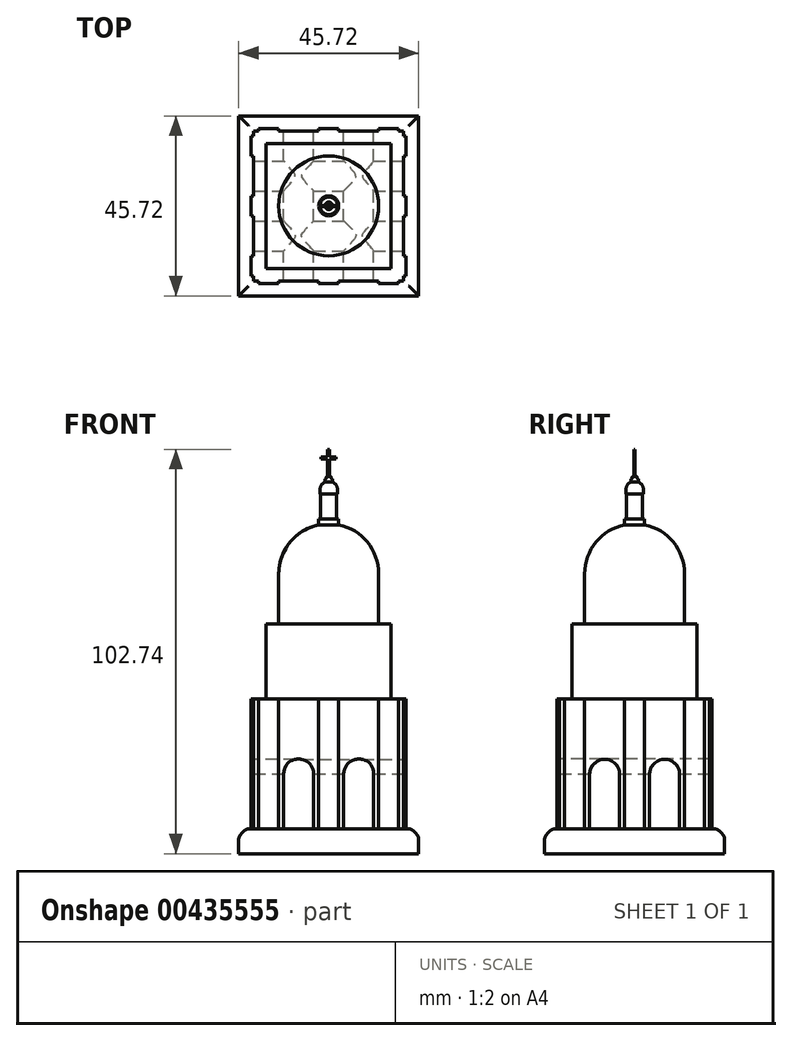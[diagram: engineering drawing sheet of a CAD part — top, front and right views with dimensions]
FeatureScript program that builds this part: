
annotation { "Feature Type Name" : "Feature", "Feature Type Description" : "" }
export const myFeature = defineFeature(function(context is Context, id is Id, definition is map)
    precondition{}
    {
        {
            var Q0;
            Q0=qCreatedBy(makeId("Top.planeOp"),FACE);
            var sketch = newSketch(context, id + "F0", { "sketchPlane" : qUnion([Q0])});
            skLineSegment(sketch, "E0.bottom", {"start": v(-19.05, -19.05) * mm, "end": v(19.05, -19.05) * mm});
            skLineSegment(sketch, "E0.top", {"start": v(-19.05, 19.05) * mm, "end": v(19.05, 19.05) * mm});
            skLineSegment(sketch, "E0.left", {"start": v(-19.05, -19.05) * mm, "end": v(-19.05, 19.05) * mm});
            skLineSegment(sketch, "E0.right", {"start": v(19.05, -19.05) * mm, "end": v(19.05, 19.05) * mm});
            skPoint(sketch, "E0.middle", {"position": v(0, 0) * mm});
            skLineSegment(sketch, "E1.bottom", {"start": v(-19.05, -19.05) * mm, "end": v(-11.43, -19.05) * mm});
            skLineSegment(sketch, "E1.left", {"start": v(-19.05, -19.05) * mm, "end": v(-19.05, -18.14) * mm});
            skLineSegment(sketch, "E2.bottom", {"start": v(-11.43, -19.05) * mm, "end": v(-3.8, -19.05) * mm});
            skLineSegment(sketch, "E3.bottom", {"start": v(-3.8, -19.05) * mm, "end": v(3.81, -19.05) * mm});
            skLineSegment(sketch, "E4.bottom", {"start": v(3.81, -19.05) * mm, "end": v(11.43, -19.05) * mm});
            skSolve(sketch);
        }
        {
            var Q0;
            Q0=makeQuery(id+"F0.imprint","IMPRINT",FACE,{"disambiguationData":[TD([[makeQuery(id+"F0.imprint","IMPRINT",EDGE,{"derivedFrom":sQuery(id+"F0.wireOp",EDGE,"E0.bottom")}),1.0]])]});
            extrude(context, id + "F1", {"entities" : qUnion([Q0]), "depth" : 38.1 * mm});
        }
        {
            var Q0;
            Q0=makeQuery(id+"F1.opExtrude","CAP_FACE",FACE,{"disambiguationData":[OSD([sQuery(id+"F0.wireOp",EDGE,"E0.bottom"),sQuery(id+"F0.wireOp",EDGE,"E0.top"),sQuery(id+"F0.wireOp",EDGE,"E0.left"),sQuery(id+"F0.wireOp",EDGE,"E0.right")])],"isStart":false});
            var sketch = newSketch(context, id + "F2", { "sketchPlane" : qUnion([Q0])});
            skLineSegment(sketch, "E5.bottom", {"start": v(-15.88, -15.88) * mm, "end": v(15.88, -15.88) * mm});
            skLineSegment(sketch, "E5.top", {"start": v(-15.88, 15.88) * mm, "end": v(15.88, 15.88) * mm});
            skLineSegment(sketch, "E5.left", {"start": v(-15.88, -15.88) * mm, "end": v(-15.88, 15.88) * mm});
            skLineSegment(sketch, "E5.right", {"start": v(15.88, -15.88) * mm, "end": v(15.88, 15.88) * mm});
            skPoint(sketch, "E5.middle", {"position": v(0, 0) * mm});
            skSolve(sketch);
        }
        {
            var Q0;
            Q0 = qSketchRegion(id + "F2", true);
            extrude(context, id + "F3", {"entities" : qUnion([Q0]), "operationType" : NewBodyOperationType.ADD, "depth" : 19.05 * mm});
        }
        {
            var Q0;
            Q0=makeQuery(id+"F3.opExtrude","CAP_FACE",FACE,{"disambiguationData":[OSD([sQuery(id+"F2.wireOp",EDGE,"E5.bottom"),sQuery(id+"F2.wireOp",EDGE,"E5.top"),sQuery(id+"F2.wireOp",EDGE,"E5.left"),sQuery(id+"F2.wireOp",EDGE,"E5.right")])],"isStart":false});
            var sketch = newSketch(context, id + "F4", { "sketchPlane" : qUnion([Q0])});
            skCircle(sketch, "E6", {"center": v(0, 0) * mm, "radius": 12.7 * mm});
            skSolve(sketch);
        }
        {
            var Q0;
            Q0 = qSketchRegion(id + "F4", true);
            extrude(context, id + "F5", {"entities" : qUnion([Q0]), "operationType" : NewBodyOperationType.ADD, "depth" : 25.4 * mm});
        }
        {
            var Q0;
            Q0=makeQuery(id+"F5.opExtrude","CAP_FACE",FACE,{"disambiguationData":[OSD([sQuery(id+"F4.wireOp",EDGE,"E6")])],"isStart":false});
            fillet(context, id + "F6", {"entities" : qUnion([Q0]), "radius" : 12.7 * mm, "tangentPropagation" : true, "allowEdgeOverflow" : false});
        }
        {
            var Q0;
            Q0=makeQuery(id+"F3.opExtrude","CAP_FACE",FACE,{"disambiguationData":[OSD([sQuery(id+"F2.wireOp",EDGE,"E5.bottom"),sQuery(id+"F2.wireOp",EDGE,"E5.top"),sQuery(id+"F2.wireOp",EDGE,"E5.left"),sQuery(id+"F2.wireOp",EDGE,"E5.right")])],"isStart":false});
            var sketch = newSketch(context, id + "F7", { "sketchPlane" : qUnion([Q0])});
            skCircle(sketch, "E7", {"center": v(0, 0) * mm, "radius": 2.54 * mm});
            skSolve(sketch);
        }
        {
            var Q0;
            Q0 = qSketchRegion(id + "F7", true);
            extrude(context, id + "F8", {"entities" : qUnion([Q0]), "operationType" : NewBodyOperationType.ADD, "depth" : 26.67 * mm});
        }
        {
            var Q0;
            Q0=makeQuery(id+"F8.opExtrude","CAP_FACE",FACE,{"disambiguationData":[OSD([sQuery(id+"F7.wireOp",EDGE,"E7")])],"isStart":false});
            var sketch = newSketch(context, id + "F9", { "sketchPlane" : qUnion([Q0])});
            skCircle(sketch, "E8", {"center": v(0, 0) * mm, "radius": 2.03 * mm});
            skSolve(sketch);
        }
        {
            var Q0;
            Q0 = qSketchRegion(id + "F9", true);
            extrude(context, id + "F10", {"entities" : qUnion([Q0]), "operationType" : NewBodyOperationType.ADD, "depth" : 6.35 * mm});
        }
        {
            var Q0;
            Q0=makeQuery(id+"F10.opExtrude","CAP_FACE",FACE,{"disambiguationData":[OSD([sQuery(id+"F9.wireOp",EDGE,"E8")])],"isStart":false});
            var sketch = newSketch(context, id + "F11", { "sketchPlane" : qUnion([Q0])});
            skCircle(sketch, "E9", {"center": v(0, 0) * mm, "radius": 2.22 * mm});
            skSolve(sketch);
        }
        {
            var Q0;
            Q0 = qSketchRegion(id + "F11", true);
            extrude(context, id + "F12", {"entities" : qUnion([Q0]), "operationType" : NewBodyOperationType.ADD, "depth" : 3.05 * mm});
        }
        {
            var Q0;
            Q0=makeQuery(id+"F12.opExtrude","CAP_FACE",FACE,{"disambiguationData":[OSD([sQuery(id+"F11.wireOp",EDGE,"E9")])],"isStart":false});
            fillet(context, id + "F13", {"entities" : qUnion([Q0]), "radius" : 1.9 * mm, "tangentPropagation" : true, "allowEdgeOverflow" : false});
        }
        {
            var Q0;
            Q0=makeQuery(id+"F12.opExtrude","CAP_FACE",FACE,{"disambiguationData":[OSD([sQuery(id+"F11.wireOp",EDGE,"E9")])],"isStart":false});
            var sketch = newSketch(context, id + "F14", { "sketchPlane" : qUnion([Q0])});
            skCircle(sketch, "E10", {"center": v(0, 0) * mm, "radius": 0.95 * mm});
            skSolve(sketch);
        }
        {
            var Q0;
            Q0 = qSketchRegion(id + "F14", true);
            extrude(context, id + "F15", {"entities" : qUnion([Q0]), "operationType" : NewBodyOperationType.ADD, "depth" : 0.76 * mm});
        }
        {
            var Q0;
            Q0=makeQuery(id+"F15.opExtrude","CAP_FACE",FACE,{"disambiguationData":[OSD([sQuery(id+"F14.wireOp",EDGE,"E10")])],"isStart":false});
            var Q1;
            Q1=makeQuery(id+"F15.opExtrude","SWEPT_FACE",FACE,{"disambiguationData":[OSD([sQuery(id+"F14.wireOp",EDGE,"E10")])]});
            fillet(context, id + "F16", {"entities" : qUnion([Q0, Q1]), "radius" : 0.25 * mm, "tangentPropagation" : true, "allowEdgeOverflow" : false});
        }
        {
            var Q0;
            Q0=makeQuery(id+"F15.opExtrude","CAP_FACE",FACE,{"disambiguationData":[OSD([sQuery(id+"F14.wireOp",EDGE,"E10")])],"isStart":false});
            var sketch = newSketch(context, id + "F17", { "sketchPlane" : qUnion([Q0])});
            skCircle(sketch, "E11", {"center": v(0, 0) * mm, "radius": 0.64 * mm});
            skSolve(sketch);
        }
        {
            var Q0;
            Q0 = qSketchRegion(id + "F17", true);
            extrude(context, id + "F18", {"entities" : qUnion([Q0]), "operationType" : NewBodyOperationType.ADD, "depth" : 0.64 * mm});
        }
        {
            var Q0;
            Q0=makeQuery(id+"F18.opExtrude","CAP_FACE",FACE,{"disambiguationData":[OSD([sQuery(id+"F17.wireOp",EDGE,"E11")])],"isStart":false});
            var Q1;
            Q1=makeQuery(id+"F18.opExtrude","SWEPT_FACE",FACE,{"disambiguationData":[OSD([sQuery(id+"F17.wireOp",EDGE,"E11")])]});
            fillet(context, id + "F19", {"entities" : qUnion([Q0, Q1]), "radius" : 0.25 * mm, "tangentPropagation" : true, "allowEdgeOverflow" : false});
        }
        {
            var Q0;
            Q0=makeQuery(id+"F18.opExtrude","CAP_FACE",FACE,{"disambiguationData":[OSD([sQuery(id+"F17.wireOp",EDGE,"E11")])],"isStart":false});
            var sketch = newSketch(context, id + "F20", { "sketchPlane" : qUnion([Q0])});
            skLineSegment(sketch, "E12.bottom", {"start": v(0.25, -0.13) * mm, "end": v(-0.25, -0.13) * mm});
            skLineSegment(sketch, "E12.top", {"start": v(0.25, 0.13) * mm, "end": v(-0.25, 0.13) * mm});
            skLineSegment(sketch, "E12.left", {"start": v(0.25, -0.13) * mm, "end": v(0.25, 0.13) * mm});
            skLineSegment(sketch, "E12.right", {"start": v(-0.25, -0.13) * mm, "end": v(-0.25, 0.13) * mm});
            skPoint(sketch, "E12.middle", {"position": v(0, 0) * mm});
            skSolve(sketch);
        }
        {
            var Q0;
            Q0 = qSketchRegion(id + "F20", true);
            extrude(context, id + "F21", {"entities" : qUnion([Q0]), "operationType" : NewBodyOperationType.ADD, "depth" : 6.86 * mm});
        }
        {
            var Q0;
            Q0=makeQuery(id+"F21.opExtrude","SWEPT_FACE",FACE,{"disambiguationData":[OSD([sQuery(id+"F20.wireOp",EDGE,"E12.bottom")])]});
            var sketch = newSketch(context, id + "F22", { "sketchPlane" : qUnion([Q0])});
            skLineSegment(sketch, "E13.bottom", {"start": v(-1.9, 99.04) * mm, "end": v(1.9, 99.04) * mm});
            skLineSegment(sketch, "E13.top", {"start": v(-1.9, 99.55) * mm, "end": v(1.9, 99.55) * mm});
            skLineSegment(sketch, "E13.left", {"start": v(-1.9, 99.04) * mm, "end": v(-1.9, 99.55) * mm});
            skLineSegment(sketch, "E13.right", {"start": v(1.9, 99.04) * mm, "end": v(1.9, 99.55) * mm});
            skPoint(sketch, "E13.middle", {"position": v(0, 99.3) * mm});
            skSolve(sketch);
        }
        {
            var Q0;
            {var subQ0=sQuery(id+"F22.wireOp",EDGE,"E13.left");Q0=makeQuery(id+"F22.imprint","IMPRINT",FACE,{"disambiguationData":[TD([[makeQuery(id+"F22.imprint","IMPRINT",EDGE,{"derivedFrom":subQ0}),-1.0]])]});}
            var Q1;
            {var subQ0=sQuery(id+"F22.wireOp",EDGE,"E13.right");Q1=makeQuery(id+"F22.imprint","IMPRINT",FACE,{"disambiguationData":[TD([[makeQuery(id+"F22.imprint","IMPRINT",EDGE,{"derivedFrom":subQ0}),1.0]])]});}
            extrude(context, id + "F23", {"entities" : qUnion([Q0, Q1]), "operationType" : NewBodyOperationType.ADD, "depth" : -0.25 * mm});
        }
        {
            var Q0;
            Q0=qCreatedBy(makeId("Top.planeOp"),FACE);
            var sketch = newSketch(context, id + "F24", { "sketchPlane" : qUnion([Q0])});
            skLineSegment(sketch, "E14.bottom", {"start": v(-11.43, -19.05) * mm, "end": v(-3.8, -19.05) * mm});
            skLineSegment(sketch, "E14.top", {"start": v(-11.43, -16.51) * mm, "end": v(-3.8, -16.51) * mm});
            skLineSegment(sketch, "E14.left", {"start": v(-11.43, -19.05) * mm, "end": v(-11.43, -16.51) * mm});
            skLineSegment(sketch, "E14.right", {"start": v(-3.8, -19.05) * mm, "end": v(-3.8, -16.51) * mm});
            skLineSegment(sketch, "E15.0", {"start": v(-3.8, -19.05) * mm, "end": v(3.81, -19.05) * mm, "construction": true});
            skLineSegment(sketch, "E16.0", {"start": v(-19.05, 19.05) * mm, "end": v(19.05, 19.05) * mm, "construction": true});
            skLineSegment(sketch, "E17", {"start": v(0, -19.05) * mm, "end": v(0, 19.05) * mm, "construction": true});
            skLineSegment(sketch, "E18.MirrorCS", {"start": v(3.8, -19.05) * mm, "end": v(3.8, -16.51) * mm});
            skLineSegment(sketch, "E19.MirrorCS", {"start": v(11.43, -16.51) * mm, "end": v(3.8, -16.51) * mm});
            skLineSegment(sketch, "E20.MirrorCS", {"start": v(11.43, -19.05) * mm, "end": v(11.43, -16.51) * mm});
            skLineSegment(sketch, "E21.MirrorCS", {"start": v(11.43, -19.05) * mm, "end": v(3.8, -19.05) * mm});
            skSolve(sketch);
        }
        {
            var Q0;
            Q0 = qSketchRegion(id + "F24", true);
            extrude(context, id + "F25", {"entities" : qUnion([Q0]), "operationType" : NewBodyOperationType.REMOVE, "oppositeDirection" : true, "depth" : -19.05 * mm});
        }
        {
            var Q0;
            Q0=makeQuery(id+"F25.boolean.opBoolean","COPY",FACE,{"derivedFrom":makeQuery(id+"F25.opExtrude","SWEPT_FACE",FACE,{"disambiguationData":[OSD([sQuery(id+"F24.wireOp",EDGE,"E14.top")])]})});
            var sketch = newSketch(context, id + "F26", { "sketchPlane" : qUnion([Q0])});
            skPoint(sketch, "E22.1.internal.snap0", {"position": v(-7.62, 19.05) * mm});
            skFitSpline(sketch, "E22", {"points": [v(-11.43, 19.05) * mm, v(-7.62, 22.78) * mm, v(-3.8, 19.05) * mm], "startDerivative": vector(0.48, 15.5) * mm, "endDerivative": vector(0.9, -14.36) * mm});
            skLineSegment(sketch, "E23", {"start": v(0, 25.4) * mm, "end": v(0, 0) * mm, "construction": true});
            skFitSpline(sketch, "E24.MirrorCS", {"points": [v(11.43, 19.05) * mm, v(7.62, 22.78) * mm, v(3.8, 19.05) * mm], "startDerivative": vector(-0.48, 15.5) * mm, "endDerivative": vector(-0.9, -14.36) * mm});
            skLineSegment(sketch, "E25.0", {"start": v(11.43, 19.05) * mm, "end": v(3.8, 19.05) * mm});
            skLineSegment(sketch, "E26.0.2", {"start": v(3.8, 19.05) * mm, "end": v(11.43, 19.05) * mm});
            skSolve(sketch);
        }
        {
            var Q0;
            Q0=makeQuery(id+"F26.imprint","IMPRINT",FACE,{"disambiguationData":[TD([[makeQuery(id+"F26.imprint","IMPRINT",EDGE,{"derivedFrom":sQuery(id+"F26.wireOp",EDGE,"E22")}),-1.0]])]});
            extrude(context, id + "F27", {"entities" : qUnion([Q0]), "operationType" : NewBodyOperationType.REMOVE, "endBound" : BoundingType.SYMMETRIC, "depth" : 76.2 * mm});
        }
        {
            var Q0;
            Q0=makeQuery(id+"F26.imprint","IMPRINT",FACE,{"disambiguationData":[TD([[makeQuery(id+"F26.imprint","IMPRINT",EDGE,{"derivedFrom":sQuery(id+"F26.wireOp",EDGE,"E24.MirrorCS")}),1.0]])]});
            extrude(context, id + "F28", {"entities" : qUnion([Q0]), "operationType" : NewBodyOperationType.REMOVE, "endBound" : BoundingType.SYMMETRIC, "oppositeDirection" : true, "depth" : 76.2 * mm});
        }
        {
            var Q0;
            Q0=makeQuery(id+"F25.boolean.opBoolean","COPY",FACE,{"derivedFrom":makeQuery(id+"F25.opExtrude","SWEPT_FACE",FACE,{"disambiguationData":[OSD([sQuery(id+"F24.wireOp",EDGE,"E14.top")])]})});
            var Q1;
            Q1=makeQuery(id+"F25.boolean.opBoolean","COPY",FACE,{"derivedFrom":makeQuery(id+"F25.opExtrude","SWEPT_FACE",FACE,{"disambiguationData":[OSD([sQuery(id+"F24.wireOp",EDGE,"E19.MirrorCS")])]})});
            extrude(context, id + "F29", {"entities" : qUnion([Q0, Q1]), "operationType" : NewBodyOperationType.REMOVE, "endBound" : BoundingType.SYMMETRIC, "oppositeDirection" : true, "depth" : 76.2 * mm});
        }
        {
            var Q0;
            Q0=makeQuery(id+"F1.opExtrude","SWEPT_FACE",FACE,{"disambiguationData":[OSD([sQuery(id+"F0.wireOp",EDGE,"E0.right")])]});
            var sketch = newSketch(context, id + "F30", { "sketchPlane" : qUnion([Q0])});
            skLineSegment(sketch, "E27", {"start": v(-19.05, 0) * mm, "end": v(-11.43, 0) * mm, "construction": true});
            skLineSegment(sketch, "E28", {"start": v(-11.43, 0) * mm, "end": v(-3.8, 0) * mm, "construction": true});
            skLineSegment(sketch, "E29", {"start": v(-3.8, 0) * mm, "end": v(3.81, 0) * mm, "construction": true});
            skLineSegment(sketch, "E30", {"start": v(3.81, 0) * mm, "end": v(11.43, 0) * mm, "construction": true});
            skLineSegment(sketch, "E31", {"start": v(11.43, 0) * mm, "end": v(19.05, 0) * mm, "construction": true});
            skLineSegment(sketch, "E32.bottom", {"start": v(-11.43, 0) * mm, "end": v(-3.8, 0) * mm});
            skLineSegment(sketch, "E32.top", {"start": v(-11.43, 19.05) * mm, "end": v(-3.8, 19.05) * mm});
            skLineSegment(sketch, "E32.left", {"start": v(-11.43, 0) * mm, "end": v(-11.43, 19.05) * mm});
            skLineSegment(sketch, "E32.right", {"start": v(-3.8, 0) * mm, "end": v(-3.8, 19.05) * mm});
            skLineSegment(sketch, "E33.bottom", {"start": v(3.81, 0) * mm, "end": v(11.43, 0) * mm});
            skPoint(sketch, "E34.2.internal.snap0", {"position": v(-7.62, 19.05) * mm});
            skFitSpline(sketch, "E34", {"points": [v(-11.43, 19.05) * mm, v(-7.62, 22.7) * mm, v(-3.8, 19.05) * mm], "startDerivative": vector(0.37, 13.04) * mm, "endDerivative": vector(0.34, -13.46) * mm});
            skFitSpline(sketch, "E35.MirrorCS", {"points": [v(11.43, 19.05) * mm, v(7.62, 22.7) * mm, v(3.8, 19.05) * mm], "startDerivative": vector(-0.37, 13.04) * mm, "endDerivative": vector(-0.34, -13.46) * mm});
            skLineSegment(sketch, "E36.MirrorCS", {"start": v(11.43, 19.05) * mm, "end": v(3.8, 19.05) * mm});
            skLineSegment(sketch, "E37.MirrorCS", {"start": v(11.43, 0) * mm, "end": v(11.43, 19.05) * mm});
            skLineSegment(sketch, "E38.MirrorCS", {"start": v(3.8, 0) * mm, "end": v(3.8, 19.05) * mm});
            skSolve(sketch);
        }
        {
            var Q0;
            Q0=makeQuery(id+"F30.imprint","IMPRINT",FACE,{"disambiguationData":[TD([[makeQuery(id+"F30.imprint","IMPRINT",EDGE,{"derivedFrom":sQuery(id+"F30.wireOp",EDGE,"E35.MirrorCS")}),1.0]])]});
            var Q1;
            Q1=makeQuery(id+"F30.imprint","IMPRINT",FACE,{"disambiguationData":[TD([[makeQuery(id+"F30.imprint","IMPRINT",EDGE,{"derivedFrom":sQuery(id+"F30.wireOp",EDGE,"E33.bottom")}),1.0]])]});
            var Q2;
            Q2=makeQuery(id+"F30.imprint","IMPRINT",FACE,{"disambiguationData":[TD([[makeQuery(id+"F30.imprint","IMPRINT",EDGE,{"derivedFrom":sQuery(id+"F30.wireOp",EDGE,"E32.top")}),1.0]])]});
            var Q3;
            Q3=makeQuery(id+"F30.imprint","IMPRINT",FACE,{"disambiguationData":[TD([[makeQuery(id+"F30.imprint","IMPRINT",EDGE,{"derivedFrom":sQuery(id+"F30.wireOp",EDGE,"E32.bottom")}),1.0]])]});
            extrude(context, id + "F31", {"entities" : qUnion([Q0, Q1, Q2, Q3]), "operationType" : NewBodyOperationType.REMOVE, "oppositeDirection" : true, "depth" : 50.8 * mm});
        }
        {
            var Q0;
            Q0=qCreatedBy(makeId("Top.planeOp"),FACE);
            var sketch = newSketch(context, id + "F32", { "sketchPlane" : qUnion([Q0])});
            skLineSegment(sketch, "E39.bottom", {"start": v(-22.86, -22.86) * mm, "end": v(22.86, -22.86) * mm});
            skLineSegment(sketch, "E39.top", {"start": v(-22.86, 22.86) * mm, "end": v(22.86, 22.86) * mm});
            skLineSegment(sketch, "E39.left", {"start": v(-22.86, -22.86) * mm, "end": v(-22.86, 22.86) * mm});
            skLineSegment(sketch, "E39.right", {"start": v(22.86, -22.86) * mm, "end": v(22.86, 22.86) * mm});
            skPoint(sketch, "E39.middle", {"position": v(0, 0) * mm});
            skSolve(sketch);
        }
        {
            var Q0;
            Q0=makeQuery(id+"F32.imprint","IMPRINT",FACE,{"disambiguationData":[TD([[makeQuery(id+"F32.imprint","IMPRINT",EDGE,{"derivedFrom":sQuery(id+"F32.wireOp",EDGE,"E39.bottom")}),1.0]])]});
            extrude(context, id + "F33", {"entities" : qUnion([Q0]), "operationType" : NewBodyOperationType.ADD, "depth" : 5.08 * mm});
        }
        {
            var Q0;
            Q0=makeQuery(id+"F33.opExtrude","CAP_EDGE",EDGE,{"disambiguationData":[OSD([sQuery(id+"F32.wireOp",EDGE,"E39.right")])],"isStart":false});
            var Q1;
            Q1=makeQuery(id+"F33.opExtrude","CAP_EDGE",EDGE,{"disambiguationData":[OSD([sQuery(id+"F32.wireOp",EDGE,"E39.top")])],"isStart":false});
            var Q2;
            Q2=makeQuery(id+"F33.opExtrude","CAP_EDGE",EDGE,{"disambiguationData":[OSD([sQuery(id+"F32.wireOp",EDGE,"E39.left")])],"isStart":false});
            var Q3;
            Q3=makeQuery(id+"F33.opExtrude","CAP_EDGE",EDGE,{"disambiguationData":[OSD([sQuery(id+"F32.wireOp",EDGE,"E39.bottom")])],"isStart":false});
            fillet(context, id + "F34", {"entities" : qUnion([Q0, Q1, Q2, Q3]), "radius" : 2.54 * mm, "tangentPropagation" : true, "rho" : .25, "crossSection" : FilletCrossSection.CONIC, "allowEdgeOverflow" : false});
        }
        {
            var Q0;
            Q0=makeQuery(id+"F1.opExtrude","SWEPT_FACE",FACE,{"disambiguationData":[OSD([sQuery(id+"F0.wireOp",EDGE,"E0.bottom"),sQuery(id+"F0.wireOp",EDGE,"E1.bottom"),sQuery(id+"F0.wireOp",EDGE,"E2.bottom"),sQuery(id+"F0.wireOp",EDGE,"E3.bottom"),sQuery(id+"F0.wireOp",EDGE,"E4.bottom")])]});
            var sketch = newSketch(context, id + "F35", { "sketchPlane" : qUnion([Q0])});
            skLineSegment(sketch, "E40", {"start": v(-11.43, 5.08) * mm, "end": v(-12.7, 5.08) * mm, "construction": true});
            skLineSegment(sketch, "E41", {"start": v(-12.7, 5.08) * mm, "end": v(-17.78, 5.08) * mm});
            skLineSegment(sketch, "E42", {"start": v(-3.8, 5.08) * mm, "end": v(-2.54, 5.08) * mm, "construction": true});
            skLineSegment(sketch, "E43", {"start": v(-2.54, 5.08) * mm, "end": v(0, 5.08) * mm});
            skLineSegment(sketch, "E44", {"start": v(-17.78, 5.08) * mm, "end": v(-17.78, 38.1) * mm});
            skLineSegment(sketch, "E45", {"start": v(-12.7, 5.08) * mm, "end": v(-12.7, 38.1) * mm});
            skLineSegment(sketch, "E46", {"start": v(-2.54, 5.08) * mm, "end": v(-2.54, 38.1) * mm});
            skLineSegment(sketch, "E47", {"start": v(0, 5.08) * mm, "end": v(0, 38.1) * mm});
            skLineSegment(sketch, "E48", {"start": v(-2.54, 38.1) * mm, "end": v(0, 38.1) * mm});
            skLineSegment(sketch, "E49", {"start": v(-12.7, 38.1) * mm, "end": v(-17.78, 38.1) * mm});
            skLineSegment(sketch, "E50.MirrorCS", {"start": v(2.54, 38.1) * mm, "end": v(0, 38.1) * mm});
            skLineSegment(sketch, "E51.MirrorCS", {"start": v(2.54, 5.08) * mm, "end": v(2.54, 38.1) * mm});
            skLineSegment(sketch, "E52.MirrorCS", {"start": v(2.54, 5.08) * mm, "end": v(0, 5.08) * mm});
            skLineSegment(sketch, "E53.MirrorCS", {"start": v(12.7, 5.08) * mm, "end": v(17.78, 5.08) * mm});
            skLineSegment(sketch, "E54.MirrorCS", {"start": v(12.7, 5.08) * mm, "end": v(12.7, 38.1) * mm});
            skLineSegment(sketch, "E55.MirrorCS", {"start": v(17.78, 5.08) * mm, "end": v(17.78, 38.1) * mm});
            skLineSegment(sketch, "E56.MirrorCS", {"start": v(12.7, 38.1) * mm, "end": v(17.78, 38.1) * mm});
            skSolve(sketch);
        }
        {
            var Q0;
            Q0=makeQuery(id+"F35.imprint","IMPRINT",FACE,{"disambiguationData":[TD([[makeQuery(id+"F35.imprint","IMPRINT",EDGE,{"derivedFrom":sQuery(id+"F35.wireOp",EDGE,"E41")}),1.0]])]});
            var Q1;
            Q1=makeQuery(id+"F35.imprint","IMPRINT",FACE,{"disambiguationData":[TD([[makeQuery(id+"F35.imprint","IMPRINT",EDGE,{"derivedFrom":sQuery(id+"F35.wireOp",EDGE,"E47")}),-1.0]])]});
            var Q2;
            Q2=makeQuery(id+"F35.imprint","IMPRINT",FACE,{"disambiguationData":[TD([[makeQuery(id+"F35.imprint","IMPRINT",EDGE,{"derivedFrom":sQuery(id+"F35.wireOp",EDGE,"E53.MirrorCS")}),1.0]])]});
            var Q3;
            Q3=makeQuery(id+"F35.imprint","IMPRINT",FACE,{"disambiguationData":[TD([[makeQuery(id+"F35.imprint","IMPRINT",EDGE,{"derivedFrom":sQuery(id+"F35.wireOp",EDGE,"E43")}),1.0]])]});
            extrude(context, id + "F36", {"entities" : qUnion([Q0, Q1, Q2, Q3]), "operationType" : NewBodyOperationType.ADD, "depth" : 0.64 * mm});
        }
        {
            var Q0;
            Q0=makeQuery(id+"F1.opExtrude","SWEPT_FACE",FACE,{"disambiguationData":[OSD([sQuery(id+"F0.wireOp",EDGE,"E0.left"),sQuery(id+"F0.wireOp",EDGE,"E1.left")])]});
            var sketch = newSketch(context, id + "F37", { "sketchPlane" : qUnion([Q0])});
            skLineSegment(sketch, "E57", {"start": v(-19.05, 5.08) * mm, "end": v(-17.78, 5.08) * mm, "construction": true});
            skLineSegment(sketch, "E58", {"start": v(-17.78, 5.08) * mm, "end": v(-12.7, 5.08) * mm});
            skLineSegment(sketch, "E59", {"start": v(-3.8, 5.08) * mm, "end": v(-2.54, 5.08) * mm, "construction": true});
            skLineSegment(sketch, "E60", {"start": v(-2.54, 5.08) * mm, "end": v(0, 5.08) * mm});
            skLineSegment(sketch, "E61", {"start": v(-17.78, 5.08) * mm, "end": v(-17.78, 38.1) * mm});
            skLineSegment(sketch, "E62", {"start": v(-12.7, 5.08) * mm, "end": v(-12.7, 38.1) * mm});
            skLineSegment(sketch, "E63", {"start": v(-17.78, 38.1) * mm, "end": v(-12.7, 38.1) * mm});
            skLineSegment(sketch, "E64", {"start": v(-2.54, 5.08) * mm, "end": v(-2.54, 38.1) * mm});
            skLineSegment(sketch, "E65", {"start": v(-2.54, 38.1) * mm, "end": v(0, 38.1) * mm});
            skLineSegment(sketch, "E66", {"start": v(0, 38.1) * mm, "end": v(0, 5.08) * mm});
            skLineSegment(sketch, "E67.MirrorCS", {"start": v(2.54, 38.1) * mm, "end": v(0, 38.1) * mm});
            skLineSegment(sketch, "E68.MirrorCS", {"start": v(2.54, 5.08) * mm, "end": v(2.54, 38.1) * mm});
            skLineSegment(sketch, "E69.MirrorCS", {"start": v(2.54, 5.08) * mm, "end": v(0, 5.08) * mm});
            skLineSegment(sketch, "E70.MirrorCS", {"start": v(17.78, 38.1) * mm, "end": v(12.7, 38.1) * mm});
            skLineSegment(sketch, "E71.MirrorCS", {"start": v(17.78, 5.08) * mm, "end": v(17.78, 38.1) * mm});
            skLineSegment(sketch, "E72.MirrorCS", {"start": v(12.7, 5.08) * mm, "end": v(12.7, 38.1) * mm});
            skLineSegment(sketch, "E73.MirrorCS", {"start": v(17.78, 5.08) * mm, "end": v(12.7, 5.08) * mm});
            skSolve(sketch);
        }
        {
            var Q0;
            Q0 = qSketchRegion(id + "F37", true);
            extrude(context, id + "F38", {"entities" : qUnion([Q0]), "operationType" : NewBodyOperationType.ADD, "depth" : 0.64 * mm});
        }
        {
            var Q0;
            Q0=makeQuery(id+"F1.opExtrude","SWEPT_FACE",FACE,{"disambiguationData":[OSD([sQuery(id+"F0.wireOp",EDGE,"E0.right")])]});
            var sketch = newSketch(context, id + "F39", { "sketchPlane" : qUnion([Q0])});
            skLineSegment(sketch, "E74", {"start": v(-19.05, 5.08) * mm, "end": v(-17.78, 5.08) * mm, "construction": true});
            skLineSegment(sketch, "E75", {"start": v(-3.8, 5.08) * mm, "end": v(-2.54, 5.08) * mm, "construction": true});
            skLineSegment(sketch, "E76", {"start": v(-17.78, 5.08) * mm, "end": v(-12.7, 5.08) * mm});
            skLineSegment(sketch, "E77", {"start": v(-2.54, 5.08) * mm, "end": v(0, 5.08) * mm});
            skLineSegment(sketch, "E78", {"start": v(-17.78, 5.08) * mm, "end": v(-17.78, 38.1) * mm});
            skLineSegment(sketch, "E79", {"start": v(-12.7, 5.08) * mm, "end": v(-12.7, 38.1) * mm});
            skLineSegment(sketch, "E80", {"start": v(-12.7, 38.1) * mm, "end": v(-17.78, 38.1) * mm});
            skLineSegment(sketch, "E81", {"start": v(-2.54, 5.08) * mm, "end": v(-2.54, 38.1) * mm});
            skLineSegment(sketch, "E82", {"start": v(-2.54, 38.1) * mm, "end": v(0, 38.1) * mm});
            skLineSegment(sketch, "E83", {"start": v(0, 38.1) * mm, "end": v(0, 5.08) * mm});
            skLineSegment(sketch, "E84.MirrorCS", {"start": v(2.54, 38.1) * mm, "end": v(0, 38.1) * mm});
            skLineSegment(sketch, "E85.MirrorCS", {"start": v(2.54, 5.08) * mm, "end": v(2.54, 38.1) * mm});
            skLineSegment(sketch, "E86.MirrorCS", {"start": v(2.54, 5.08) * mm, "end": v(0, 5.08) * mm});
            skLineSegment(sketch, "E87.MirrorCS", {"start": v(12.7, 5.08) * mm, "end": v(12.7, 38.1) * mm});
            skLineSegment(sketch, "E88.MirrorCS", {"start": v(17.78, 5.08) * mm, "end": v(17.78, 38.1) * mm});
            skLineSegment(sketch, "E89.MirrorCS", {"start": v(12.7, 38.1) * mm, "end": v(17.78, 38.1) * mm});
            skLineSegment(sketch, "E90.MirrorCS", {"start": v(17.78, 5.08) * mm, "end": v(12.7, 5.08) * mm});
            skSolve(sketch);
        }
        {
            var Q0;
            Q0=makeQuery(id+"F39.imprint","IMPRINT",FACE,{"disambiguationData":[TD([[makeQuery(id+"F39.imprint","IMPRINT",EDGE,{"derivedFrom":sQuery(id+"F39.wireOp",EDGE,"E83")}),1.0]])]});
            var Q1;
            Q1=makeQuery(id+"F39.imprint","IMPRINT",FACE,{"disambiguationData":[TD([[makeQuery(id+"F39.imprint","IMPRINT",EDGE,{"derivedFrom":sQuery(id+"F39.wireOp",EDGE,"E77")}),1.0]])]});
            var Q2;
            Q2=makeQuery(id+"F39.imprint","IMPRINT",FACE,{"disambiguationData":[TD([[makeQuery(id+"F39.imprint","IMPRINT",EDGE,{"derivedFrom":sQuery(id+"F39.wireOp",EDGE,"E76")}),1.0]])]});
            var Q3;
            Q3=makeQuery(id+"F39.imprint","IMPRINT",FACE,{"disambiguationData":[TD([[makeQuery(id+"F39.imprint","IMPRINT",EDGE,{"derivedFrom":sQuery(id+"F39.wireOp",EDGE,"E87.MirrorCS")}),-1.0]])]});
            extrude(context, id + "F40", {"entities" : qUnion([Q0, Q1, Q2, Q3]), "operationType" : NewBodyOperationType.ADD, "depth" : 0.64 * mm});
        }
        {
            var Q0;
            Q0=makeQuery(id+"F1.opExtrude","SWEPT_FACE",FACE,{"disambiguationData":[OSD([sQuery(id+"F0.wireOp",EDGE,"E0.top")])]});
            var sketch = newSketch(context, id + "F41", { "sketchPlane" : qUnion([Q0])});
            skLineSegment(sketch, "E91", {"start": v(-19.05, 5.08) * mm, "end": v(-17.78, 5.08) * mm, "construction": true});
            skLineSegment(sketch, "E92", {"start": v(-17.78, 5.08) * mm, "end": v(-12.7, 5.08) * mm});
            skLineSegment(sketch, "E93", {"start": v(-3.8, 5.08) * mm, "end": v(-2.54, 5.08) * mm, "construction": true});
            skLineSegment(sketch, "E94", {"start": v(-2.54, 5.08) * mm, "end": v(0, 5.08) * mm});
            skLineSegment(sketch, "E95", {"start": v(-2.54, 5.08) * mm, "end": v(-2.54, 38.1) * mm});
            skLineSegment(sketch, "E96", {"start": v(-2.54, 38.1) * mm, "end": v(0, 38.1) * mm});
            skLineSegment(sketch, "E97", {"start": v(0, 38.1) * mm, "end": v(0, 5.08) * mm});
            skLineSegment(sketch, "E98", {"start": v(-12.7, 5.08) * mm, "end": v(-12.7, 38.1) * mm});
            skLineSegment(sketch, "E99", {"start": v(-12.7, 38.1) * mm, "end": v(-17.78, 38.1) * mm});
            skLineSegment(sketch, "E100", {"start": v(-17.78, 38.1) * mm, "end": v(-17.78, 5.08) * mm});
            skLineSegment(sketch, "E101.MirrorCS", {"start": v(2.54, 38.1) * mm, "end": v(0, 38.1) * mm});
            skLineSegment(sketch, "E102.MirrorCS", {"start": v(2.54, 5.08) * mm, "end": v(2.54, 38.1) * mm});
            skLineSegment(sketch, "E103.MirrorCS", {"start": v(2.54, 5.08) * mm, "end": v(0, 5.08) * mm});
            skLineSegment(sketch, "E104.MirrorCS", {"start": v(12.7, 5.08) * mm, "end": v(12.7, 38.1) * mm});
            skLineSegment(sketch, "E105.MirrorCS", {"start": v(17.78, 5.08) * mm, "end": v(12.7, 5.08) * mm});
            skLineSegment(sketch, "E106.MirrorCS", {"start": v(17.78, 38.1) * mm, "end": v(17.78, 5.08) * mm});
            skLineSegment(sketch, "E107.MirrorCS", {"start": v(12.7, 38.1) * mm, "end": v(17.78, 38.1) * mm});
            skSolve(sketch);
        }
        {
            var Q0;
            Q0=makeQuery(id+"F41.imprint","IMPRINT",FACE,{"disambiguationData":[TD([[makeQuery(id+"F41.imprint","IMPRINT",EDGE,{"derivedFrom":sQuery(id+"F41.wireOp",EDGE,"E92")}),-1.0]])]});
            var Q1;
            Q1=makeQuery(id+"F41.imprint","IMPRINT",FACE,{"disambiguationData":[TD([[makeQuery(id+"F41.imprint","IMPRINT",EDGE,{"derivedFrom":sQuery(id+"F41.wireOp",EDGE,"E94")}),-1.0]])]});
            var Q2;
            Q2=makeQuery(id+"F41.imprint","IMPRINT",FACE,{"disambiguationData":[TD([[makeQuery(id+"F41.imprint","IMPRINT",EDGE,{"derivedFrom":sQuery(id+"F41.wireOp",EDGE,"E97")}),1.0]])]});
            var Q3;
            Q3=makeQuery(id+"F41.imprint","IMPRINT",FACE,{"disambiguationData":[TD([[makeQuery(id+"F41.imprint","IMPRINT",EDGE,{"derivedFrom":sQuery(id+"F41.wireOp",EDGE,"E104.MirrorCS")}),-1.0]])]});
            extrude(context, id + "F42", {"entities" : qUnion([Q0, Q1, Q2, Q3]), "operationType" : NewBodyOperationType.ADD, "depth" : 0.64 * mm});
        }
        {
            var Q0;
            {var subQ4=makeQuery(id+"F31.opExtrude","SWEPT_FACE",FACE,{"disambiguationData":[OSD([sQuery(id+"F30.wireOp",EDGE,"E32.right")])]});var subQ5=sQuery(id+"F24.wireOp",EDGE,"E14.right");var subQ8=makeQuery(id+"F25.boolean.opBoolean","COPY",FACE,{"derivedFrom":makeQuery(id+"F25.opExtrude","SWEPT_FACE",FACE,{"disambiguationData":[OSD([subQ5])]})});var subQ10=sQuery(id+"F0.wireOp",EDGE,"E0.top");var subQ11=makeQuery(id+"F1.opExtrude","SWEPT_FACE",FACE,{"disambiguationData":[OSD([subQ10])]});var subQ12=sQuery(id+"F0.wireOp",EDGE,"E4.bottom");var subQ13=sQuery(id+"F0.wireOp",EDGE,"E3.bottom");var subQ14=sQuery(id+"F0.wireOp",EDGE,"E2.bottom");var subQ15=sQuery(id+"F0.wireOp",EDGE,"E1.bottom");var subQ16=sQuery(id+"F0.wireOp",EDGE,"E0.bottom");var subQ18=sQuery(id+"F0.wireOp",EDGE,"E1.left");var subQ19=sQuery(id+"F0.wireOp",EDGE,"E0.right");var subQ20=sQuery(id+"F0.wireOp",EDGE,"E0.left");var subQ21=makeQuery(id+"F1.opExtrude","CAP_FACE",FACE,{"disambiguationData":[OSD([subQ16,subQ10,subQ20,subQ19,subQ15,subQ18,subQ14,subQ13,subQ12])],"isStart":true});var subQ22=makeQuery(id+"F29.boolean.opBoolean","SPLIT",FACE,{"disambiguationData":[TD([subQ8])],"derivedFrom":subQ21});var subQ24=makeQuery(id+"F31.opExtrude","SWEPT_FACE",FACE,{"disambiguationData":[OSD([sQuery(id+"F30.wireOp",EDGE,"E32.left")])]});var subQ28=makeQuery(id+"F1.opExtrude","SWEPT_FACE",FACE,{"disambiguationData":[OSD([subQ19])]});var subQ29=makeQuery(id+"F29.boolean.opBoolean","SPLIT",FACE,{"disambiguationData":[TD([subQ28])],"derivedFrom":subQ21});var subQ30=sQuery(id+"F24.wireOp",EDGE,"E14.left");var subQ32=makeQuery(id+"F25.boolean.opBoolean","COPY",FACE,{"derivedFrom":makeQuery(id+"F25.opExtrude","SWEPT_FACE",FACE,{"disambiguationData":[OSD([subQ30])]})});var subQ34=makeQuery(id+"F29.boolean.opBoolean","SPLIT",FACE,{"disambiguationData":[TD([subQ32])],"derivedFrom":subQ21});Q0=makeQuery(id+"F33.boolean.opBoolean","MERGE",FACE,{"derivedFrom":[makeQuery(id+"F31.boolean.opBoolean","SPLIT",FACE,{"disambiguationData":[TD([subQ24])],"derivedFrom":subQ34}),makeQuery(id+"F31.boolean.opBoolean","SPLIT",FACE,{"disambiguationData":[TD([subQ11])],"derivedFrom":subQ34}),makeQuery(id+"F31.boolean.opBoolean","SPLIT",FACE,{"disambiguationData":[TD([subQ4])],"derivedFrom":subQ34}),makeQuery(id+"F31.boolean.opBoolean","SPLIT",FACE,{"disambiguationData":[TD([subQ24])],"derivedFrom":subQ29}),makeQuery(id+"F31.boolean.opBoolean","SPLIT",FACE,{"disambiguationData":[TD([subQ11])],"derivedFrom":subQ29}),makeQuery(id+"F31.boolean.opBoolean","SPLIT",FACE,{"disambiguationData":[TD([subQ4])],"derivedFrom":subQ29}),makeQuery(id+"F31.boolean.opBoolean","SPLIT",FACE,{"disambiguationData":[TD([subQ24])],"derivedFrom":subQ22}),makeQuery(id+"F31.boolean.opBoolean","SPLIT",FACE,{"disambiguationData":[TD([subQ11])],"derivedFrom":subQ22}),makeQuery(id+"F31.boolean.opBoolean","SPLIT",FACE,{"disambiguationData":[TD([subQ4])],"derivedFrom":subQ22}),makeQuery(id+"F33.opExtrude","CAP_FACE",FACE,{"disambiguationData":[OSD([sQuery(id+"F32.wireOp",EDGE,"E39.bottom"),sQuery(id+"F32.wireOp",EDGE,"E39.top"),sQuery(id+"F32.wireOp",EDGE,"E39.left"),sQuery(id+"F32.wireOp",EDGE,"E39.right")])],"isStart":true})]});}
            extrude(context, id + "F43", {"entities" : qUnion([Q0]), "operationType" : NewBodyOperationType.ADD, "depth" : 1.27 * mm});
        }
    });
